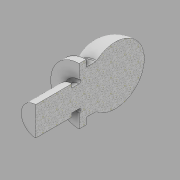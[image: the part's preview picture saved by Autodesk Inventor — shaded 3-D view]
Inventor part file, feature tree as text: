
AUTODESK INVENTOR PART (.ipt)
format: ipt  version: 2020 (Build 240168000, 168)  size: 146,944 bytes
history: native  units: in
note: dims shown in document units (in); Inventor stores cm internally (conversion verified against a paired STEP export)
features: fillet x2, other x1, revolve x1, sketch x1
ambient origin geometry x8: Origin, YZ Plane, XZ Plane, XY Plane, X Axis, Y Axis, Z Axis, Center Point
bodies: Body1 (feature_tree)
feature tree (5):
  other  "Sólido1"
  revolve  "Revolución1"  [1 undecoded]
  fillet  "Empalme1"  Radius=0.375in
  fillet  "Empalme2"  Radius=0.5in
  sketch  "Boceto1"  dims[d0=0.25in d1=0.49in d2=0.375in d3=0.5in d4=0.313in d5=0.375in d7=0.688in d8=0.435in d9=0.016in d10=0.032in d11=0.375in d12=90.0deg d13=0.016in d14=0.016in]
note: 1 required parameter value undecoded (feature->parameter linkage not recoverable at this tier; creation-order binding heuristic only, values carry confidence <= 0.55)
